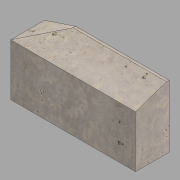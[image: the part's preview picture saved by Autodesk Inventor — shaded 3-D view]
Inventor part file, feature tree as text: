
AUTODESK INVENTOR PART (.ipt)
format: ipt  version: 2022.1 (Build 261234020, 234B)  size: 131,072 bytes
history: native  units: in
note: dims shown in document units (in); Inventor stores cm internally (conversion verified against a paired STEP export)
features: extrude x3, sketch x3
ambient origin geometry x8: Origin, YZ Plane, XZ Plane, XY Plane, X Axis, Y Axis, Z Axis, Center Point
bodies: Solid1 (feature_tree)
feature tree (6):
  extrude  "Extrusion1"  Depth=6.5in
  extrude  "Extrusion2"  Depth=12.0in
  extrude  "Extrusion3"  TaperAngle=0.0deg  [1 undecoded]
  sketch  "Sketch1"  dims[d0=24.0in d1=6.5in]
  sketch  "Sketch2"  dims[d2=12.0in d3=0.0in d4=2.0in]
  sketch  "Sketch3"  dims[d5=6.0in d6=0.0in d7=0.0in d8=6.0in d9=2.0in d10=0.0in d11=0.0in]
note: 1 required parameter value undecoded (feature->parameter linkage not recoverable at this tier; creation-order binding heuristic only, values carry confidence <= 0.55)
